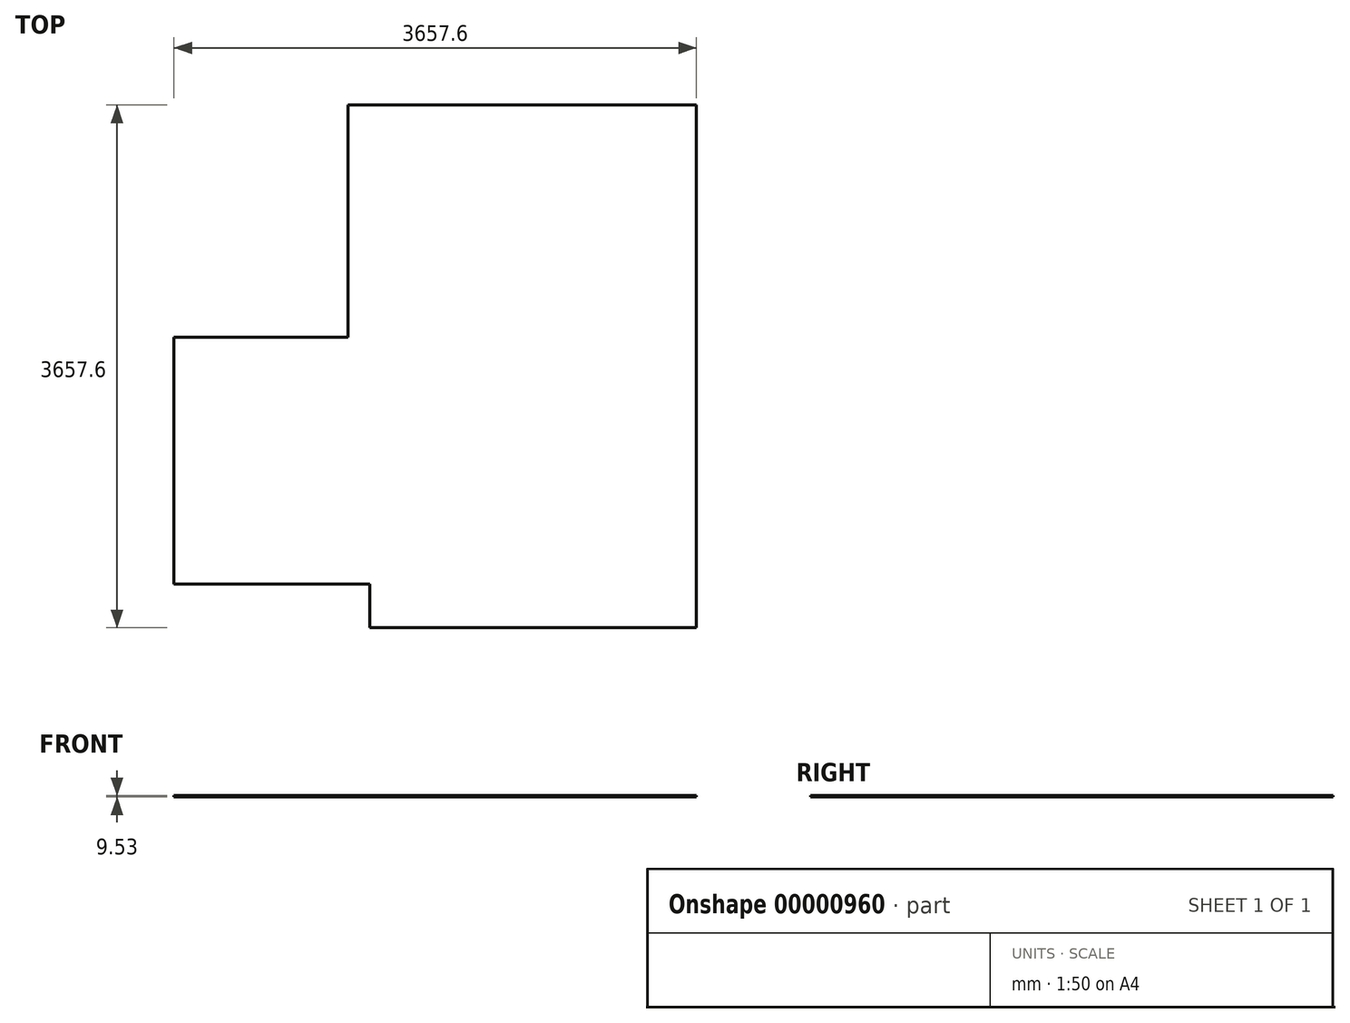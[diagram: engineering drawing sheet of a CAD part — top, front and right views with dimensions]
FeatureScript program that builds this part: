
annotation { "Feature Type Name" : "Feature", "Feature Type Description" : "" }
export const myFeature = defineFeature(function(context is Context, id is Id, definition is map)
    precondition{}
    {
        {
            var Q0;
            Q0=qCreatedBy(makeId("Top.planeOp"),FACE);
            var sketch = newSketch(context, id + "F0", { "sketchPlane" : qUnion([Q0])});
            skLineSegment(sketch, "E0.bottom", {"start": v(1219.2, 3657.6) * mm, "end": v(3657.6, 3657.6) * mm});
            skLineSegment(sketch, "E0.top", {"start": v(1371.6, 0) * mm, "end": v(3657.6, 0) * mm});
            skLineSegment(sketch, "E0.left", {"start": v(0, 2032) * mm, "end": v(0, 304.8) * mm});
            skLineSegment(sketch, "E0.right", {"start": v(3657.6, 3657.6) * mm, "end": v(3657.6, 0) * mm});
            skLineSegment(sketch, "E1", {"start": v(1219.2, 2032) * mm, "end": v(1219.2, 3657.6) * mm});
            skLineSegment(sketch, "E2", {"start": v(0, 2032) * mm, "end": v(1219.2, 2032) * mm});
            skPoint(sketch, "E2.endSnap0", {"position": v(1219.2, 2032) * mm});
            skPoint(sketch, "E3.orphan", {"position": v(2648.61, 2032) * mm});
            skLineSegment(sketch, "E4", {"start": v(0, 304.8) * mm, "end": v(1371.6, 304.8) * mm});
            skLineSegment(sketch, "E5", {"start": v(1371.6, 304.8) * mm, "end": v(1371.6, 0) * mm});
            skSolve(sketch);
        }
        {
            var Q0;
            Q0 = qSketchRegion(id + "F0", true);
            extrude(context, id + "F1", {"entities" : qUnion([Q0]), "depth" : 9.52 * mm});
        }
    });
